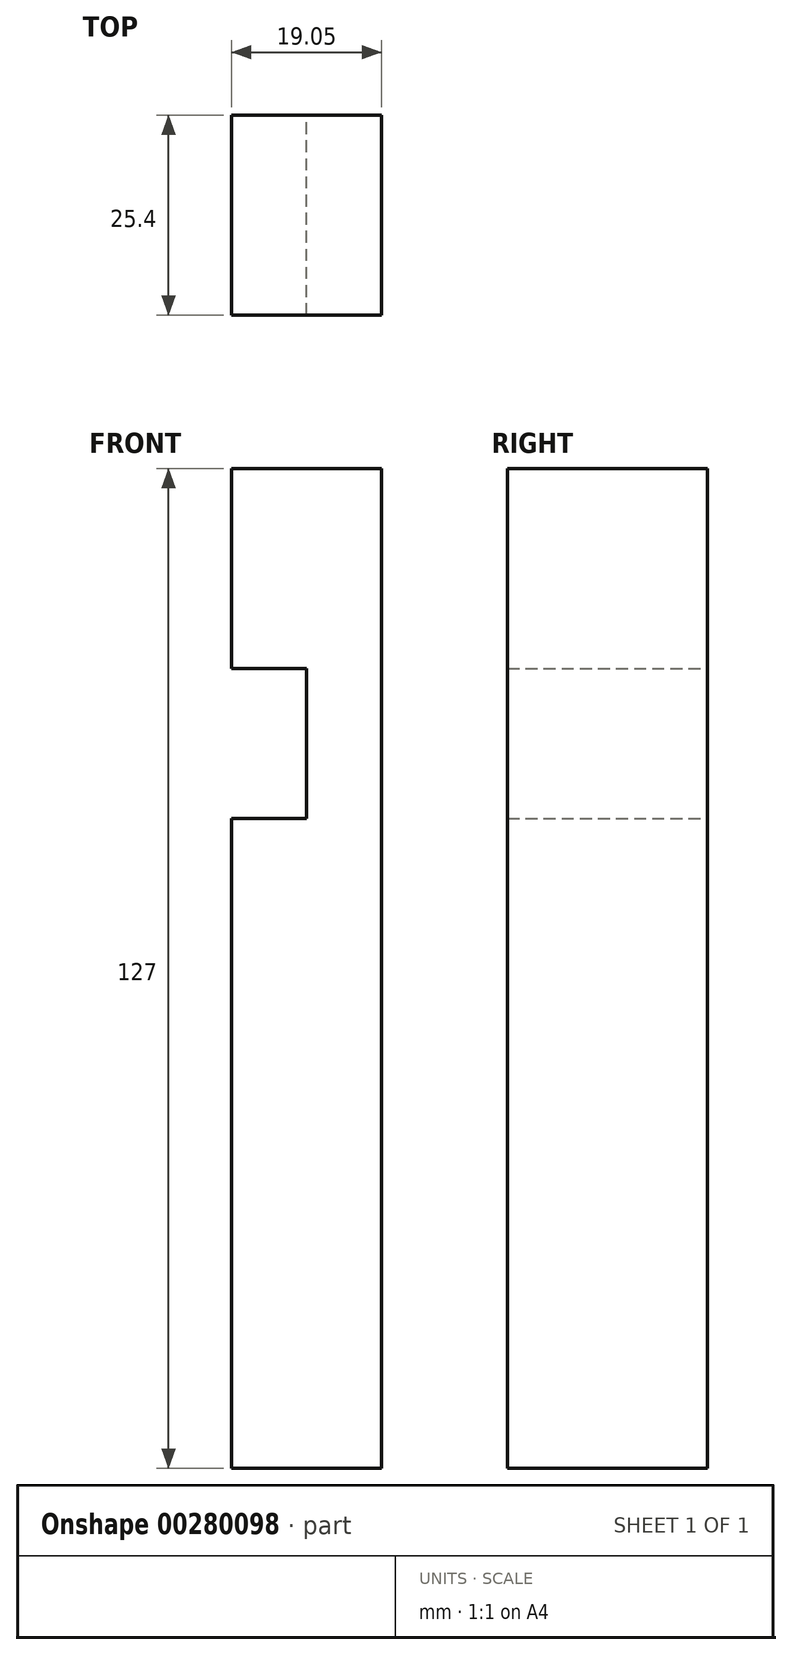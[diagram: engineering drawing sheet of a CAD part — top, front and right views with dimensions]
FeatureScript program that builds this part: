
annotation { "Feature Type Name" : "Feature", "Feature Type Description" : "" }
export const myFeature = defineFeature(function(context is Context, id is Id, definition is map)
    precondition{}
    {
        {
            var Q0;
            Q0=qCreatedBy(makeId("Front.planeOp"),FACE);
            var sketch = newSketch(context, id + "F0", { "sketchPlane" : qUnion([Q0])});
            skLineSegment(sketch, "E0", {"start": v(-30.09, 0) * mm, "end": v(-30.09, 127) * mm});
            skLineSegment(sketch, "E1", {"start": v(-30.09, 127) * mm, "end": v(-49.14, 127) * mm});
            skLineSegment(sketch, "E2", {"start": v(-49.14, 127) * mm, "end": v(-49.14, 101.6) * mm});
            skLineSegment(sketch, "E3", {"start": v(-49.14, 101.6) * mm, "end": v(-39.61, 101.6) * mm});
            skLineSegment(sketch, "E4", {"start": v(-39.61, 101.6) * mm, "end": v(-39.61, 82.55) * mm});
            skLineSegment(sketch, "E5", {"start": v(-39.61, 82.55) * mm, "end": v(-49.14, 82.55) * mm});
            skLineSegment(sketch, "E6", {"start": v(-49.14, 82.55) * mm, "end": v(-49.14, 0) * mm});
            skLineSegment(sketch, "E7", {"start": v(-30.09, 0) * mm, "end": v(-49.14, 0) * mm});
            skSolve(sketch);
        }
        {
            var Q0;
            Q0 = qSketchRegion(id + "F0", true);
            extrude(context, id + "F1", {"entities" : qUnion([Q0]), "depth" : 25.4 * mm});
        }
    });
